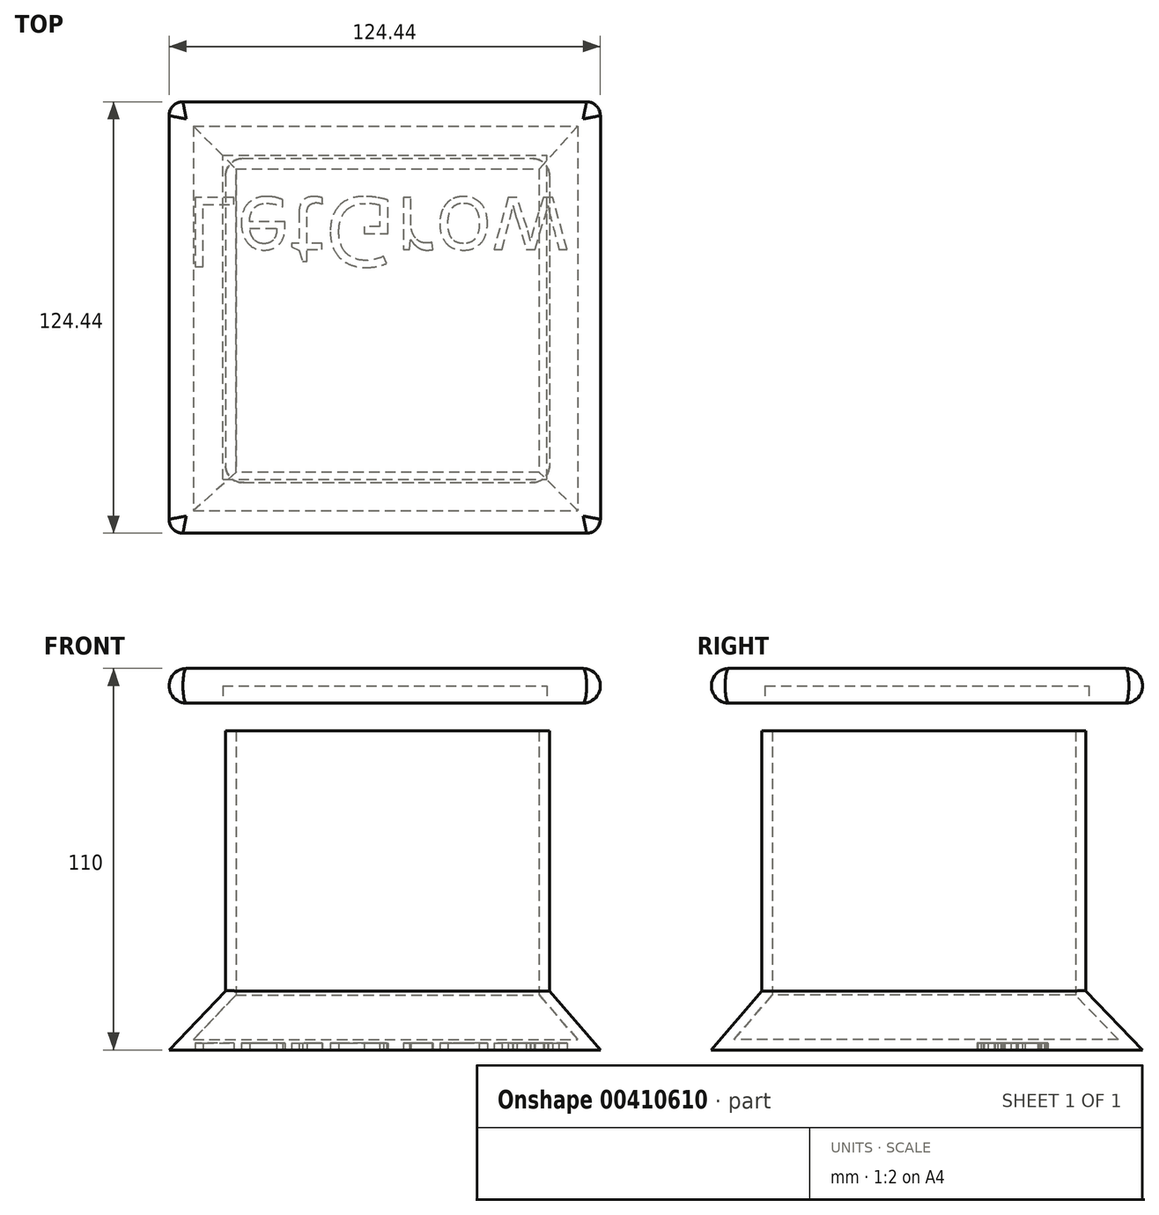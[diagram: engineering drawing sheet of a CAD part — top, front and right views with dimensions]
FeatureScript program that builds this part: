
annotation { "Feature Type Name" : "Feature", "Feature Type Description" : "" }
export const myFeature = defineFeature(function(context is Context, id is Id, definition is map)
    precondition{}
    {
        {
            var Q0;
            Q0=qCreatedBy(makeId("Top.planeOp"),FACE);
            var sketch = newSketch(context, id + "F0", { "sketchPlane" : qUnion([Q0])});
            skLineSegment(sketch, "E0.bottom", {"start": v(-62.22, 62.22) * mm, "end": v(62.22, 62.22) * mm});
            skLineSegment(sketch, "E0.top", {"start": v(-62.22, -62.22) * mm, "end": v(62.22, -62.22) * mm});
            skLineSegment(sketch, "E0.left", {"start": v(-62.22, 62.22) * mm, "end": v(-62.22, -62.22) * mm});
            skLineSegment(sketch, "E0.right", {"start": v(62.22, 62.22) * mm, "end": v(62.22, -62.22) * mm});
            skSolve(sketch);
        }
        {
            var Q0;
            Q0=qCreatedBy(makeId("Top.planeOp"),FACE);
            cPlane(context, id + "F1", {"entities" : qUnion([Q0]), "cplaneType" : CPlaneType.OFFSET, "offset" : 17 * mm, "width" : 150 * mm, "height" : 150 * mm});
        }
        {
            var Q0;
            Q0=qCreatedBy(id+"F1.planeOp",FACE);
            var sketch = newSketch(context, id + "F2", { "sketchPlane" : qUnion([Q0])});
            skLineSegment(sketch, "E1.bottom", {"start": v(-45.93, 45.85) * mm, "end": v(47.54, 45.85) * mm});
            skLineSegment(sketch, "E1.top", {"start": v(-45.93, -47.62) * mm, "end": v(47.54, -47.62) * mm});
            skLineSegment(sketch, "E1.left", {"start": v(-45.93, 45.85) * mm, "end": v(-45.93, -47.62) * mm});
            skLineSegment(sketch, "E1.right", {"start": v(47.54, 45.85) * mm, "end": v(47.54, -47.62) * mm});
            skSolve(sketch);
        }
        {
            var Q0;
            Q0=makeQuery(id+"F2.imprint","IMPRINT",FACE,{"disambiguationData":[TD([[makeQuery(id+"F2.imprint","IMPRINT",EDGE,{"derivedFrom":sQuery(id+"F2.wireOp",EDGE,"E1.bottom")}),-1.0]])]});
            var Q1;
            Q1=makeQuery(id+"F0.imprint","IMPRINT",FACE,{"disambiguationData":[TD([[makeQuery(id+"F0.imprint","IMPRINT",EDGE,{"derivedFrom":sQuery(id+"F0.wireOp",EDGE,"E0.bottom")}),-1.0]])]});
            loft(context, id + "F3", {"sheetProfilesArray" : [{ "sheetProfileEntities" : qUnion([Q0]) }, { "sheetProfileEntities" : qUnion([Q1]) }]});
        }
        {
            var Q0;
            Q0=makeQuery(id+"F3.opLoft","CAP_FACE",FACE,{"disambiguationData":[OSD([makeQuery(id+"F2.imprint","IMPRINT",FACE,{"disambiguationData":[TD([[makeQuery(id+"F2.imprint","IMPRINT",EDGE,{"derivedFrom":sQuery(id+"F2.wireOp",EDGE,"E1.bottom")}),-1.0]])]})])],"isStart":true});
            extrude(context, id + "F4", {"entities" : qUnion([Q0]), "operationType" : NewBodyOperationType.ADD, "depth" : 75 * mm});
        }
        {
            var Q0;
            Q0=makeQuery(id+"F4.opExtrude","CAP_FACE",FACE,{"disambiguationData":[OSD([makeQuery(id+"F2.imprint","IMPRINT",FACE,{"disambiguationData":[TD([[makeQuery(id+"F2.imprint","IMPRINT",EDGE,{"derivedFrom":sQuery(id+"F2.wireOp",EDGE,"E1.bottom")}),-1.0]])]})])],"isStart":false});
            shell(context, id + "F5", {"entities" : qUnion([Q0]), "thickness" : 3 * mm});
        }
        {
            var Q0;
            Q0=qCreatedBy(makeId("Top.planeOp"),FACE);
            cPlane(context, id + "F6", {"entities" : qUnion([Q0]), "cplaneType" : CPlaneType.OFFSET, "offset" : 100 * mm, "width" : 150 * mm, "height" : 150 * mm});
        }
        {
            var Q0;
            Q0=qCreatedBy(id+"F6.planeOp",FACE);
            var sketch = newSketch(context, id + "F7", { "sketchPlane" : qUnion([Q0])});
            skLineSegment(sketch, "E2.bottom", {"start": v(-62.22, 62.22) * mm, "end": v(62.22, 62.22) * mm});
            skLineSegment(sketch, "E2.top", {"start": v(-62.22, -62.22) * mm, "end": v(62.22, -62.22) * mm});
            skLineSegment(sketch, "E2.left", {"start": v(-62.22, 62.22) * mm, "end": v(-62.22, -62.22) * mm});
            skLineSegment(sketch, "E2.right", {"start": v(62.22, 62.22) * mm, "end": v(62.22, -62.22) * mm});
            skSolve(sketch);
        }
        {
            var Q0;
            Q0=makeQuery(id+"F7.imprint","IMPRINT",FACE,{"disambiguationData":[TD([[makeQuery(id+"F7.imprint","IMPRINT",EDGE,{"derivedFrom":sQuery(id+"F7.wireOp",EDGE,"E2.bottom")}),-1.0]])]});
            var Q1;
            Q1=sQuery(id+"F7.wireOp",EDGE,"E2.right");
            var Q2;
            Q2=sQuery(id+"F7.wireOp",EDGE,"E2.bottom");
            var Q3;
            Q3=sQuery(id+"F7.wireOp",EDGE,"E2.left");
            var Q4;
            Q4=sQuery(id+"F7.wireOp",EDGE,"E2.top");
            extrude(context, id + "F8", {"entities" : qUnion([Q0]), "operationType" : NewBodyOperationType.ADD, "surfaceEntities" : qUnion([Q1, Q2, Q3, Q4]), "depth" : 10 * mm});
        }
        {
            var Q0;
            Q0=makeQuery(id+"F8.opExtrude","CAP_FACE",FACE,{"disambiguationData":[OSD([sQuery(id+"F7.wireOp",EDGE,"E2.bottom"),sQuery(id+"F7.wireOp",EDGE,"E2.top"),sQuery(id+"F7.wireOp",EDGE,"E2.left"),sQuery(id+"F7.wireOp",EDGE,"E2.right")])],"isStart":true});
            var sketch = newSketch(context, id + "F9", { "sketchPlane" : qUnion([Q0])});
            skLineSegment(sketch, "E3.bottom", {"start": v(-46.74, 46.74) * mm, "end": v(46.74, 46.74) * mm});
            skLineSegment(sketch, "E3.top", {"start": v(-46.74, -46.74) * mm, "end": v(46.74, -46.74) * mm});
            skLineSegment(sketch, "E3.left", {"start": v(-46.74, 46.74) * mm, "end": v(-46.74, -46.74) * mm});
            skLineSegment(sketch, "E3.right", {"start": v(46.74, 46.74) * mm, "end": v(46.74, -46.74) * mm});
            skSolve(sketch);
        }
        {
            var Q0;
            Q0=makeQuery(id+"F9.imprint","IMPRINT",FACE,{"disambiguationData":[TD([[makeQuery(id+"F9.imprint","IMPRINT",EDGE,{"derivedFrom":sQuery(id+"F9.wireOp",EDGE,"E3.bottom")}),-1.0]])]});
            extrude(context, id + "F10", {"entities" : qUnion([Q0]), "operationType" : NewBodyOperationType.REMOVE, "oppositeDirection" : true, "depth" : 5 * mm});
        }
        {
            var Q0;
            Q0=makeQuery(id+"F8.opExtrude","CAP_EDGE",EDGE,{"disambiguationData":[OSD([sQuery(id+"F7.wireOp",EDGE,"E2.top")])],"isStart":false});
            var Q1;
            Q1=makeQuery(id+"F8.opExtrude","CAP_EDGE",EDGE,{"disambiguationData":[OSD([sQuery(id+"F7.wireOp",EDGE,"E2.right")])],"isStart":false});
            var Q2;
            Q2=makeQuery(id+"F8.opExtrude","CAP_EDGE",EDGE,{"disambiguationData":[OSD([sQuery(id+"F7.wireOp",EDGE,"E2.bottom")])],"isStart":false});
            var Q3;
            Q3=makeQuery(id+"F8.opExtrude","CAP_EDGE",EDGE,{"disambiguationData":[OSD([sQuery(id+"F7.wireOp",EDGE,"E2.left")])],"isStart":false});
            fillet(context, id + "F11", {"entities" : qUnion([Q0, Q1, Q2, Q3]), "radius" : 5 * mm, "tangentPropagation" : true, "allowEdgeOverflow" : false});
        }
        {
            var Q0;
            Q0=makeQuery(id+"F8.opExtrude","CAP_EDGE",EDGE,{"disambiguationData":[OSD([sQuery(id+"F7.wireOp",EDGE,"E2.bottom")])],"isStart":true});
            var Q1;
            Q1=makeQuery(id+"F8.opExtrude","CAP_EDGE",EDGE,{"disambiguationData":[OSD([sQuery(id+"F7.wireOp",EDGE,"E2.right")])],"isStart":true});
            var Q2;
            Q2=makeQuery(id+"F8.opExtrude","CAP_EDGE",EDGE,{"disambiguationData":[OSD([sQuery(id+"F7.wireOp",EDGE,"E2.top")])],"isStart":true});
            var Q3;
            Q3=makeQuery(id+"F8.opExtrude","CAP_EDGE",EDGE,{"disambiguationData":[OSD([sQuery(id+"F7.wireOp",EDGE,"E2.left")])],"isStart":true});
            fillet(context, id + "F12", {"entities" : qUnion([Q0, Q1, Q2, Q3]), "radius" : 5 * mm, "tangentPropagation" : true, "allowEdgeOverflow" : false});
        }
        {
            var Q0;
            Q0=makeQuery(id+"F11.opFillet","BLEND_EDGE",EDGE,{"blendedFrom":[makeQuery(id+"F8.opExtrude","CAP_EDGE",EDGE,{"disambiguationData":[OSD([sQuery(id+"F7.wireOp",EDGE,"E2.bottom")])],"isStart":false}),makeQuery(id+"F8.opExtrude","CAP_EDGE",EDGE,{"disambiguationData":[OSD([sQuery(id+"F7.wireOp",EDGE,"E2.right")])],"isStart":false})],"blendedInto":[]});
            var Q1;
            Q1=makeQuery(id+"F12.opFillet","BLEND_EDGE",EDGE,{"blendedFrom":[makeQuery(id+"F8.opExtrude","CAP_EDGE",EDGE,{"disambiguationData":[OSD([sQuery(id+"F7.wireOp",EDGE,"E2.bottom")])],"isStart":true}),makeQuery(id+"F8.opExtrude","CAP_EDGE",EDGE,{"disambiguationData":[OSD([sQuery(id+"F7.wireOp",EDGE,"E2.right")])],"isStart":true})],"blendedInto":[]});
            var Q2;
            Q2=makeQuery(id+"F11.opFillet","BLEND_EDGE",EDGE,{"blendedFrom":[makeQuery(id+"F8.opExtrude","CAP_EDGE",EDGE,{"disambiguationData":[OSD([sQuery(id+"F7.wireOp",EDGE,"E2.top")])],"isStart":false}),makeQuery(id+"F8.opExtrude","CAP_EDGE",EDGE,{"disambiguationData":[OSD([sQuery(id+"F7.wireOp",EDGE,"E2.right")])],"isStart":false})],"blendedInto":[]});
            var Q3;
            Q3=makeQuery(id+"F12.opFillet","BLEND_EDGE",EDGE,{"blendedFrom":[makeQuery(id+"F8.opExtrude","CAP_EDGE",EDGE,{"disambiguationData":[OSD([sQuery(id+"F7.wireOp",EDGE,"E2.top")])],"isStart":true}),makeQuery(id+"F8.opExtrude","CAP_EDGE",EDGE,{"disambiguationData":[OSD([sQuery(id+"F7.wireOp",EDGE,"E2.right")])],"isStart":true})],"blendedInto":[]});
            var Q4;
            Q4=makeQuery(id+"F11.opFillet","BLEND_EDGE",EDGE,{"blendedFrom":[makeQuery(id+"F8.opExtrude","CAP_EDGE",EDGE,{"disambiguationData":[OSD([sQuery(id+"F7.wireOp",EDGE,"E2.top")])],"isStart":false}),makeQuery(id+"F8.opExtrude","CAP_EDGE",EDGE,{"disambiguationData":[OSD([sQuery(id+"F7.wireOp",EDGE,"E2.left")])],"isStart":false})],"blendedInto":[]});
            var Q5;
            Q5=makeQuery(id+"F12.opFillet","BLEND_EDGE",EDGE,{"blendedFrom":[makeQuery(id+"F8.opExtrude","CAP_EDGE",EDGE,{"disambiguationData":[OSD([sQuery(id+"F7.wireOp",EDGE,"E2.top")])],"isStart":true}),makeQuery(id+"F8.opExtrude","CAP_EDGE",EDGE,{"disambiguationData":[OSD([sQuery(id+"F7.wireOp",EDGE,"E2.left")])],"isStart":true})],"blendedInto":[]});
            var Q6;
            Q6=makeQuery(id+"F11.opFillet","BLEND_EDGE",EDGE,{"blendedFrom":[makeQuery(id+"F8.opExtrude","CAP_EDGE",EDGE,{"disambiguationData":[OSD([sQuery(id+"F7.wireOp",EDGE,"E2.bottom")])],"isStart":false}),makeQuery(id+"F8.opExtrude","CAP_EDGE",EDGE,{"disambiguationData":[OSD([sQuery(id+"F7.wireOp",EDGE,"E2.left")])],"isStart":false})],"blendedInto":[]});
            var Q7;
            Q7=makeQuery(id+"F12.opFillet","BLEND_EDGE",EDGE,{"blendedFrom":[makeQuery(id+"F8.opExtrude","CAP_EDGE",EDGE,{"disambiguationData":[OSD([sQuery(id+"F7.wireOp",EDGE,"E2.bottom")])],"isStart":true}),makeQuery(id+"F8.opExtrude","CAP_EDGE",EDGE,{"disambiguationData":[OSD([sQuery(id+"F7.wireOp",EDGE,"E2.left")])],"isStart":true})],"blendedInto":[]});
            fillet(context, id + "F13", {"entities" : qUnion([Q0, Q1, Q2, Q3, Q4, Q5, Q6, Q7]), "radius" : 4 * mm, "tangentPropagation" : true, "allowEdgeOverflow" : false});
        }
        {
            var Q0;
            Q0=makeQuery(id+"F3.opLoft","CAP_FACE",FACE,{"disambiguationData":[OSD([makeQuery(id+"F0.imprint","IMPRINT",FACE,{"disambiguationData":[TD([[makeQuery(id+"F0.imprint","IMPRINT",EDGE,{"derivedFrom":sQuery(id+"F0.wireOp",EDGE,"E0.bottom")}),-1.0]])]})])],"isStart":true});
            var sketch = newSketch(context, id + "F14", { "sketchPlane" : qUnion([Q0])});
            skText(sketch, "E4", { "text": "LetGrow", "fontName": "OpenSans-Regular.ttf"});
            const initialGuessF14  = {"E4": [-0.0574, -0.03462, 1, 0, 0.0201]};
            skSetInitialGuess(sketch, initialGuessF14);
            skSolve(sketch);
        }
        {
            var Q0;
            Q0 = qSketchRegion(id + "F14", true);
            extrude(context, id + "F15", {"entities" : qUnion([Q0]), "operationType" : NewBodyOperationType.REMOVE, "oppositeDirection" : true, "depth" : 2 * mm});
        }
        {
            var Q0;
            Q0=makeQuery(id+"F3.opLoft","SWEPT_EDGE",EDGE,{"disambiguationData":[OSD([sQuery(id+"F0.wireOp",EDGE,"E0.top"),sQuery(id+"F0.wireOp",EDGE,"E0.left"),sQuery(id+"F2.wireOp",EDGE,"E1.top"),sQuery(id+"F2.wireOp",EDGE,"E1.left")])]});
            var Q1;
            Q1=makeQuery(id+"F3.opLoft","SWEPT_EDGE",EDGE,{"disambiguationData":[OSD([sQuery(id+"F0.wireOp",EDGE,"E0.bottom"),sQuery(id+"F0.wireOp",EDGE,"E0.left"),sQuery(id+"F2.wireOp",EDGE,"E1.bottom"),sQuery(id+"F2.wireOp",EDGE,"E1.left")])]});
            var Q2;
            Q2=makeQuery(id+"F3.opLoft","SWEPT_EDGE",EDGE,{"disambiguationData":[OSD([sQuery(id+"F0.wireOp",EDGE,"E0.bottom"),sQuery(id+"F0.wireOp",EDGE,"E0.right"),sQuery(id+"F2.wireOp",EDGE,"E1.bottom"),sQuery(id+"F2.wireOp",EDGE,"E1.right")])]});
            var Q3;
            Q3=makeQuery(id+"F3.opLoft","SWEPT_EDGE",EDGE,{"disambiguationData":[OSD([sQuery(id+"F0.wireOp",EDGE,"E0.top"),sQuery(id+"F0.wireOp",EDGE,"E0.right"),sQuery(id+"F2.wireOp",EDGE,"E1.top"),sQuery(id+"F2.wireOp",EDGE,"E1.right")])]});
            fillet(context, id + "F16", {"entities" : qUnion([Q0, Q1, Q2, Q3]), "radius" : 7 * mm, "tangentPropagation" : true, "allowEdgeOverflow" : false});
        }
        {
            var Q0;
            Q0=makeQuery(id+"F4.opExtrude","SWEPT_EDGE",EDGE,{"disambiguationData":[OSD([sQuery(id+"F2.wireOp",EDGE,"E1.top"),sQuery(id+"F2.wireOp",EDGE,"E1.left")])]});
            var Q1;
            Q1=makeQuery(id+"F4.opExtrude","SWEPT_EDGE",EDGE,{"disambiguationData":[OSD([sQuery(id+"F2.wireOp",EDGE,"E1.top"),sQuery(id+"F2.wireOp",EDGE,"E1.right")])]});
            var Q2;
            Q2=makeQuery(id+"F4.opExtrude","SWEPT_EDGE",EDGE,{"disambiguationData":[OSD([sQuery(id+"F2.wireOp",EDGE,"E1.bottom"),sQuery(id+"F2.wireOp",EDGE,"E1.left")])]});
            var Q3;
            Q3=makeQuery(id+"F4.opExtrude","SWEPT_EDGE",EDGE,{"disambiguationData":[OSD([sQuery(id+"F2.wireOp",EDGE,"E1.bottom"),sQuery(id+"F2.wireOp",EDGE,"E1.right")])]});
            fillet(context, id + "F17", {"entities" : qUnion([Q0, Q1, Q2, Q3]), "radius" : 5 * mm, "tangentPropagation" : true, "allowEdgeOverflow" : false});
        }
    });
